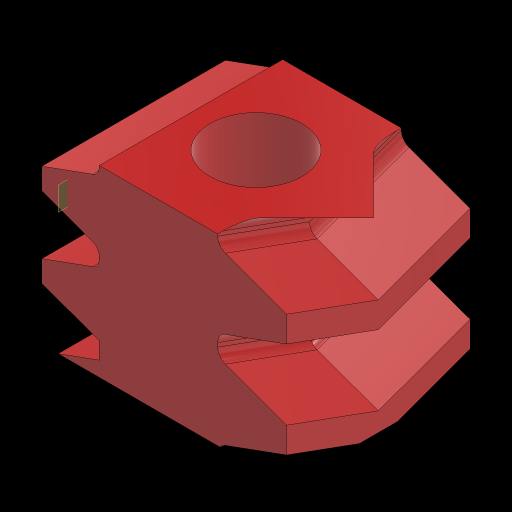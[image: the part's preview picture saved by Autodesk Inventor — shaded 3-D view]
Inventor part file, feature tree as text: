
AUTODESK INVENTOR PART (.ipt)
format: ipt  version: 2023.2 (Build 272271030, 271C)  size: 498,688 bytes
history: native  units: mm
features: sketch x5, extrude x3, projected_geometry x3, plane x2, sweep x1, pattern_linear x1, mirror x1
ambient origin geometry x8: Origin, YZ Plane, XZ Plane, XY Plane, X Axis, Y Axis, Z Axis, Center Point
bodies: Solid1 (feature_tree)
feature tree (16):
  extrude  "Extrusion1"  Depth=9.0mm
  sweep  "Sweep1"
  pattern_linear  "Rectangular Pattern2"  Spacing1=1.5mm  [1 undecoded]
  mirror  "Mirror2"
  plane  "Work Plane3"
  extrude  "Extrusion4"  Depth=4.5mm
  plane  "Work Plane4"
  extrude  "Extrusion5"  TaperAngle=0.0deg  [1 undecoded]
  sketch  "Sketch1"  dims[d0=12.0mm d1=9.0mm]
  sketch  "Sketch2"  dims[d2=4.5mm d3=0.0mm d14=12.217305mm]
  projected_geometry  "Projected Loop1"
  sketch  "Sketch3"  dims[d15=4.712389mm]
  projected_geometry  "Projected Loop2"
  sketch  "Sketch6"  dims[d16=0.57mm]
  projected_geometry  "Projected Loop5"
  sketch  "Sketch7"  dims[d17=3.375mm d18=1.5mm d19=2.356194mm d22=0.0mm d23=0.0mm d27=80.0mm d29=4.7124mm d31=3.490659mm d32=3.577925mm d48=2.356194mm d49=-1.5mm d50=12.217305mm d51=1.25mm d52=1.5625mm d53=1.963495mm d54=0.475mm d55=40.0mm d57=22.5deg d58=10.0mm d60=10.0mm d62=10.0mm d63=0.0mm d64=-1.25mm d65=4.5mm d66=0.0mm d67=0.0mm]
note: 2 required parameter values undecoded (feature->parameter linkage not recoverable at this tier; creation-order binding heuristic only, values carry confidence <= 0.55)
